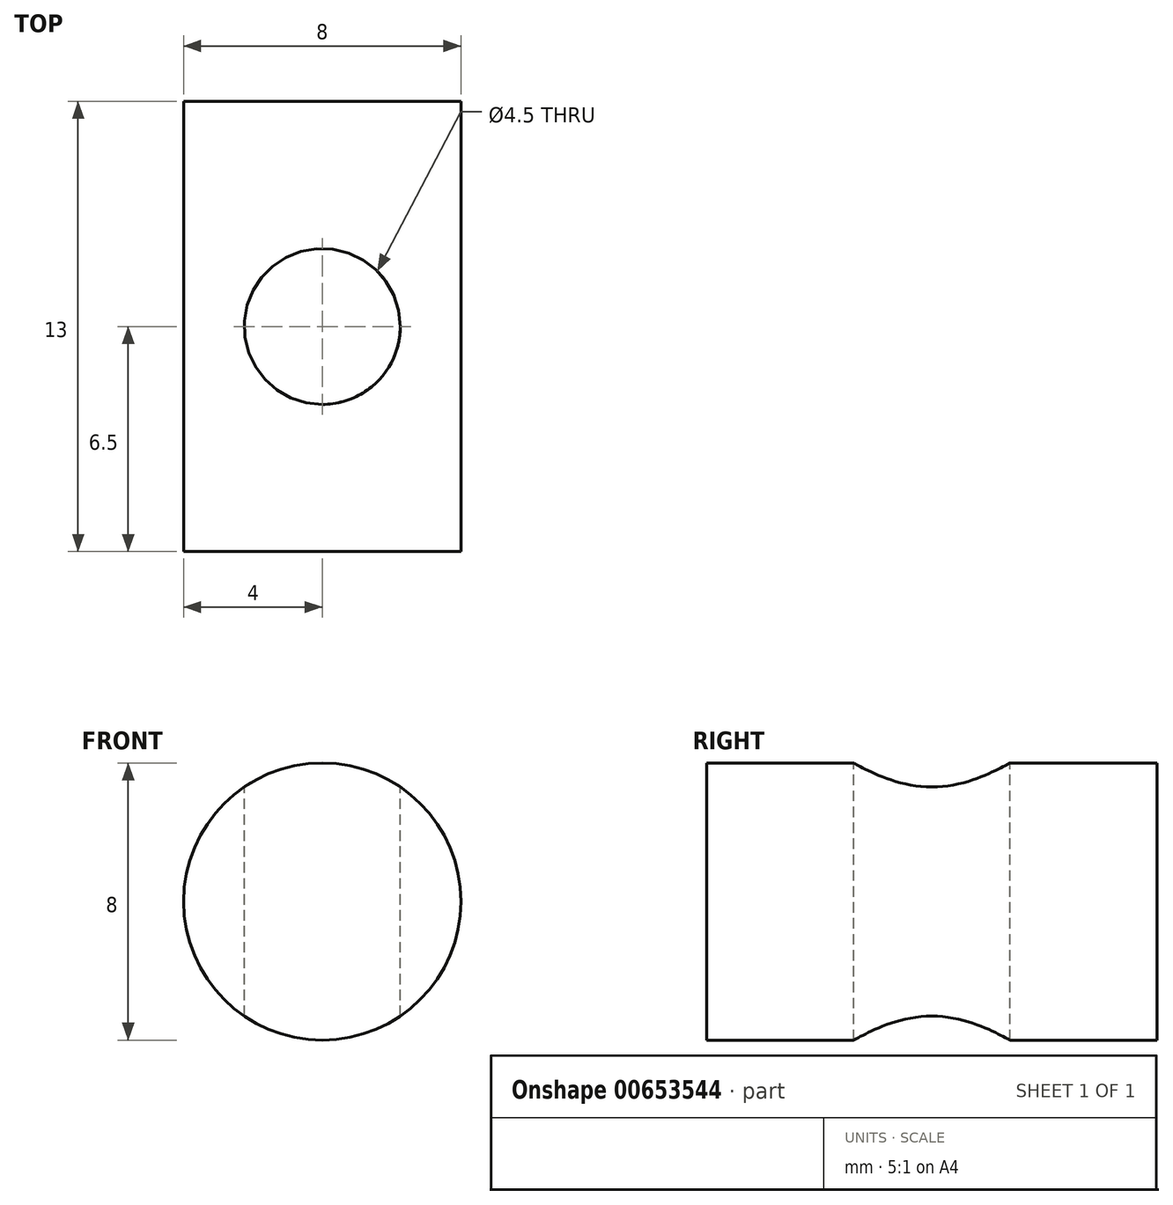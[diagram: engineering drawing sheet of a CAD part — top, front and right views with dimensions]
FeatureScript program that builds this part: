
annotation { "Feature Type Name" : "Feature", "Feature Type Description" : "" }
export const myFeature = defineFeature(function(context is Context, id is Id, definition is map)
    precondition{}
    {
        {
            var Q0;
            Q0=qCreatedBy(makeId("Front.planeOp"),FACE);
            var sketch = newSketch(context, id + "F0", { "sketchPlane" : qUnion([Q0])});
            skCircle(sketch, "E0", {"center": v(0, 0) * mm, "radius": 4 * mm});
            skSolve(sketch);
        }
        {
            var Q0;
            Q0 = qSketchRegion(id + "F0", true);
            extrude(context, id + "F1", {"entities" : qUnion([Q0]), "endBound" : BoundingType.SYMMETRIC, "depth" : 13 * mm, "offsetDistance" : 25 * mm});
        }
        {
            var Q0;
            Q0=qCreatedBy(makeId("Top.planeOp"),FACE);
            var sketch = newSketch(context, id + "F2", { "sketchPlane" : qUnion([Q0])});
            skCircle(sketch, "E1", {"center": v(0, 0) * mm, "radius": 2.25 * mm});
            skSolve(sketch);
        }
        {
            var Q0;
            Q0 = qSketchRegion(id + "F2", true);
            extrude(context, id + "F3", {"entities" : qUnion([Q0]), "operationType" : NewBodyOperationType.REMOVE, "endBound" : BoundingType.SYMMETRIC, "oppositeDirection" : true, "depth" : 25 * mm, "offsetDistance" : 25 * mm});
        }
    });
